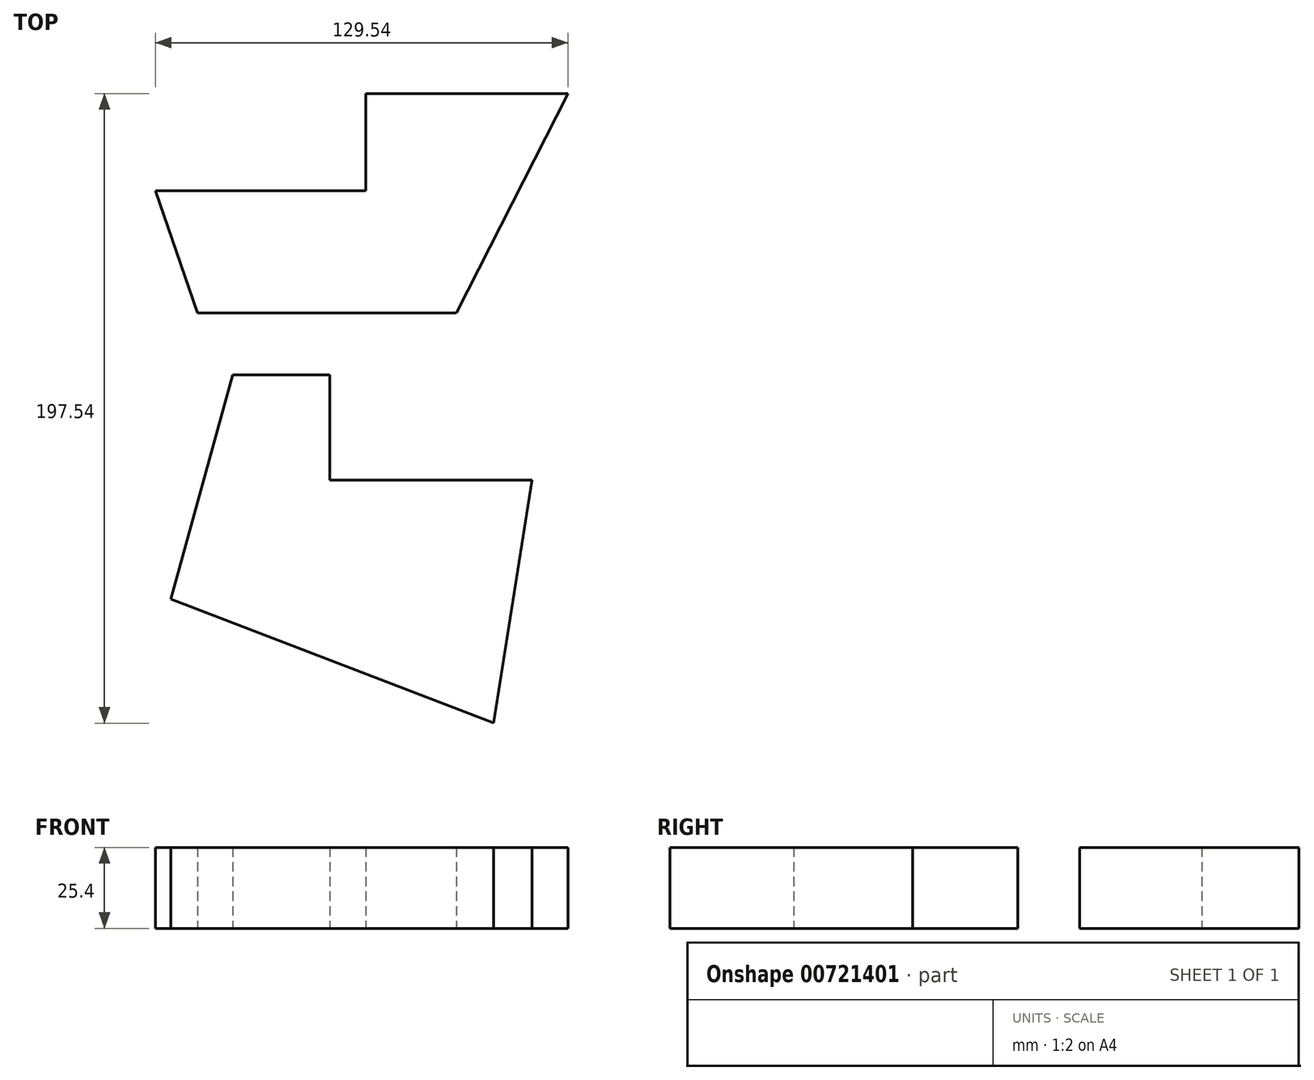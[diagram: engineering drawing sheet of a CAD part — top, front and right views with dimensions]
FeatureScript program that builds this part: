
annotation { "Feature Type Name" : "Feature", "Feature Type Description" : "" }
export const myFeature = defineFeature(function(context is Context, id is Id, definition is map)
    precondition{}
    {
        {
            var Q0;
            Q0=qCreatedBy(makeId("Top.planeOp"),FACE);
            var sketch = newSketch(context, id + "F0", { "sketchPlane" : qUnion([Q0])});
            skLineSegment(sketch, "E0", {"start": v(-50.56, 19.45) * mm, "end": v(30.72, 19.45) * mm});
            skLineSegment(sketch, "E1", {"start": v(30.72, 19.45) * mm, "end": v(65.77, 88.25) * mm});
            skLineSegment(sketch, "E2", {"start": v(65.77, 88.25) * mm, "end": v(2.27, 88.25) * mm});
            skLineSegment(sketch, "E3", {"start": v(2.27, 88.25) * mm, "end": v(2.27, 57.77) * mm});
            skLineSegment(sketch, "E4", {"start": v(2.27, 57.77) * mm, "end": v(-63.77, 57.77) * mm});
            skLineSegment(sketch, "E5", {"start": v(-63.77, 57.77) * mm, "end": v(-50.56, 19.45) * mm});
            skSolve(sketch);
        }
        {
            var Q0;
            Q0 = qSketchRegion(id + "F0", true);
            extrude(context, id + "F1", {"entities" : qUnion([Q0]), "depth" : 25.4 * mm, "offsetDistance" : 25.4 * mm});
        }
        {
            var Q0;
            Q0=qCreatedBy(makeId("Top.planeOp"),FACE);
            var sketch = newSketch(context, id + "F2", { "sketchPlane" : qUnion([Q0])});
            skLineSegment(sketch, "E6", {"start": v(-39.5, 0) * mm, "end": v(-9.02, 0) * mm});
            skLineSegment(sketch, "E7", {"start": v(-9.02, 0) * mm, "end": v(-9.02, -33.02) * mm});
            skLineSegment(sketch, "E8", {"start": v(-9.02, -33.02) * mm, "end": v(54.48, -33.02) * mm});
            skLineSegment(sketch, "E9", {"start": v(54.48, -33.02) * mm, "end": v(42.4, -109.29) * mm});
            skLineSegment(sketch, "E10", {"start": v(42.4, -109.29) * mm, "end": v(42.4, -50.5) * mm, "construction": true});
            skLineSegment(sketch, "E11", {"start": v(42.4, -109.29) * mm, "end": v(-58.85, -70.42) * mm});
            skLineSegment(sketch, "E12", {"start": v(-58.85, -70.42) * mm, "end": v(-39.5, 0) * mm});
            skLineSegment(sketch, "E13", {"start": v(-58.85, -70.42) * mm, "end": v(25.23, -70.42) * mm, "construction": true});
            skSolve(sketch);
        }
        {
            var Q0;
            Q0 = qSketchRegion(id + "F2", true);
            extrude(context, id + "F3", {"entities" : qUnion([Q0]), "depth" : 25.4 * mm, "offsetDistance" : 25.4 * mm});
        }
    });
